# Revit family: PRD_AR_FlshCntrlDvcs_ActuatorPlate_ACSF400111
name_source: partatom
category: Plumbing Fixtures
units: mm (PartAtom-declared; Revit-internal decimal feet)

## family parameters
Cut with Voids When Loaded = Yes
Enable Cutting in Views = No
Host = Face
Maintain Annotation Orientation = No
OmniClass Number = 23.45.05.14.99
OmniClass Title = Other Sanitary Washing Plumbing Fixtures
Part Type = Normal
Room Calculation Point = No
Round Connector Dimension = Use Diameter
Shared = No

## types (1)
- ACSF4001
    AssetType = Fixed
    BIMObjectName = PRD_AR_FlushControlDevices_ActuatorPlate_ACSF4001
    BuiltInFittingModel = Finishing section
    ButtonMaterial = PRD_AR_ChromatedBrass_HighPolished
    CasingMaterial = PRD_AR_StainlessSteel_Brushed
    Category = Pr_75_50_46_31, Flush control devices
    CloseOffRating = 0.0 Pa
    CoverPlateHeight = 140 mm
    CoverPlateWidth = 190 mm
    Default Elevation = 1000 mm  [stored 3.28084 ft]
    Description = Stainless steel actuator plate for concealed cistern in the AQUAFIX installation frame. Especially suitable for facilities at risk of vandalism. Actuation button for single flush with start/stop, mounting from the front with safety screws.
    Export Type to IFC As = IfcValveType
    Features = Material casing stainless steel with satin finish, dimension plate 190 x 140 mm.
    Finish = Satin finished
    FlowCoefficient = 0
    FlushingRate = 0.0 L/s
    FunctionalPrinciple = Manual
    HasIntegralShutOffDevice = No
    IfcExportAs = IfcValveType
    IfcExportType = FLUSHING
    IsHighPressure = No
    Manufacturer = KWC Group Management AG
    ManufacturerName = KWC Group Management AG
    ManufacturerURL = www.kwc-professional.com
    Material = stainless steel
    MaterialCasing = Stainless Steel
    MaterialCodeCasing = 1.4301 Chrome Nickel steel V2A
    Model = ACSF4001
    ModelNumber = 2030068181
    ModelReference = ACSF4001
    NBSDescription = Flush control devices
    NBSReference = 90-15-35/470
    Name = Actuator plate ACSF4001
    NominalDepth = 134 mm
    NominalHeight = 140 mm  [stored 0.459318 ft]
    NominalWidth = 190 mm
    OverallHeight = 0 mm  [stored 0 ft]
    OverallLength = 0 mm  [stored 0 ft]
    OverallWidth = 0 mm  [stored 0 ft]
    ProductInformation = http://pim.kwc.com
    Status = New
    SurfaceFinish = Satin Finished
    SurfaceFinishCasing = Brushed
    TestPressure = 0.0 Pa
    TtypeOfFlushingFitting = for WC cistern
    Type IFC Predefined Type = FLUSHING
    URL = www.kwc-professional.com
    Uniclass2015Code = Pr_75_50_46_31
    Uniclass2015Title = Flush control devices
    Uniclass2015Version = Products v1.36
    ValveMechanism = OTHER
    ValveOperation = PNEUMATIC
    ValvePattern = OTHER
    Version = 1
    WorkingPressure = 0.0 Pa

note: [stored X ft] marks values corroborated as IEEE doubles in the binary element streams (Revit-internal decimal feet)

## geometry (parser evidence)
native form markers: Sweep x5
no freeform markers — native parametric forms only
